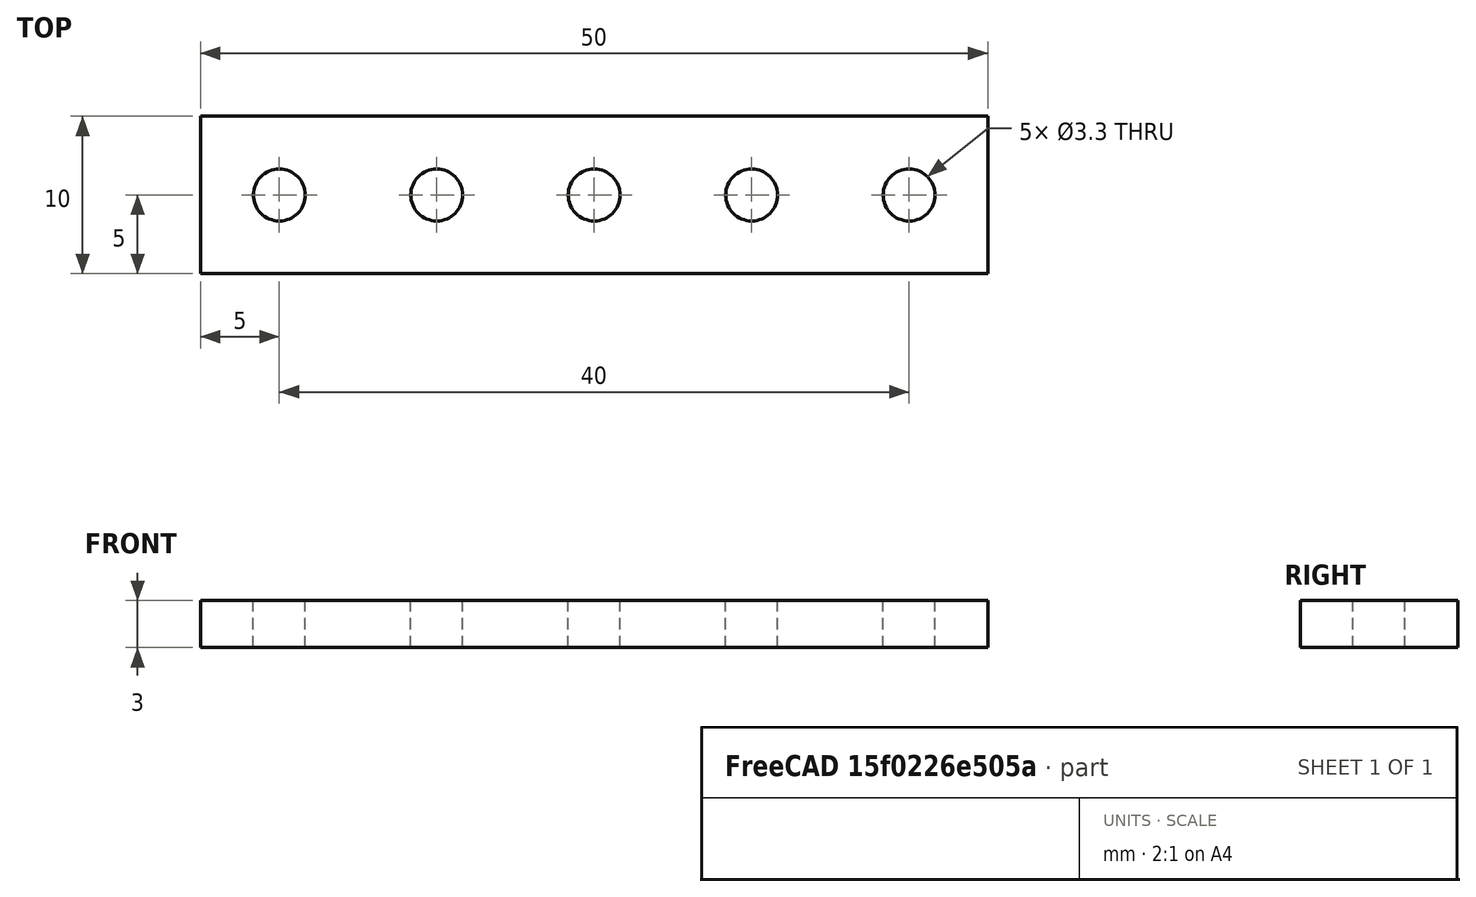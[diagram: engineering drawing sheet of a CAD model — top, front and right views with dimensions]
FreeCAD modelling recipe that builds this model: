
FCSTD DOCUMENT  (FreeCAD 0.16R6707 (Git))
Label: 02-Pieza-mecano
License: All rights reserved
LicenseURL: http://en.wikipedia.org/wiki/All_rights_reserved
objects: Part::Cylinder×5, Part::Box×1, Part::MultiFuse×1, Part::Cut×1
note: 8 computed .brp shape members not serialized (recipe doc carries the construction recipe); baked Part::Feature solids carry a one-line shape summary decoded from their .brp

FEATURE [Part::Box] Box  label="Base"
  Height = 3
  Length = 50
  Width = 10
FEATURE [Part::Cylinder] Cylinder  label="taladro1"
  Angle = 360
  Height = 10
  Placement = pos=(5,5,-4) rot=(0,0,1;0rad)
  Radius = 1.65
  expr: Radius = 3.3 / 2
FEATURE [Part::Cylinder] Cylinder001  label="taladro002"
  Angle = 360
  Height = 10
  Placement = pos=(15,5,-4) rot=(0,0,1;0rad)
  Radius = 1.65
  expr: Radius = 3.3 / 2
FEATURE [Part::Cylinder] Cylinder002  label="taladro003"
  Angle = 360
  Height = 10
  Placement = pos=(25,5,-4) rot=(0,0,1;0rad)
  Radius = 1.65
  expr: Radius = 3.3 / 2
FEATURE [Part::Cylinder] Cylinder003  label="taladro004"
  Angle = 360
  Height = 10
  Placement = pos=(35,5,-4) rot=(0,0,1;0rad)
  Radius = 1.65
  expr: Radius = 3.3 / 2
FEATURE [Part::Cylinder] Cylinder004  label="taladro005"
  Angle = 360
  Height = 10
  Placement = pos=(45,5,-4) rot=(0,0,1;0rad)
  Radius = 1.65
  expr: Radius = 3.3 / 2
FEATURE [Part::MultiFuse] Fusion  label="Taladros"
  Shapes = -> [Cylinder,Cylinder001,Cylinder002,Cylinder003,Cylinder004]
FEATURE [Part::Cut] Cut  label="Pieza-final"
  Base = -> Box
  Tool = -> Fusion
